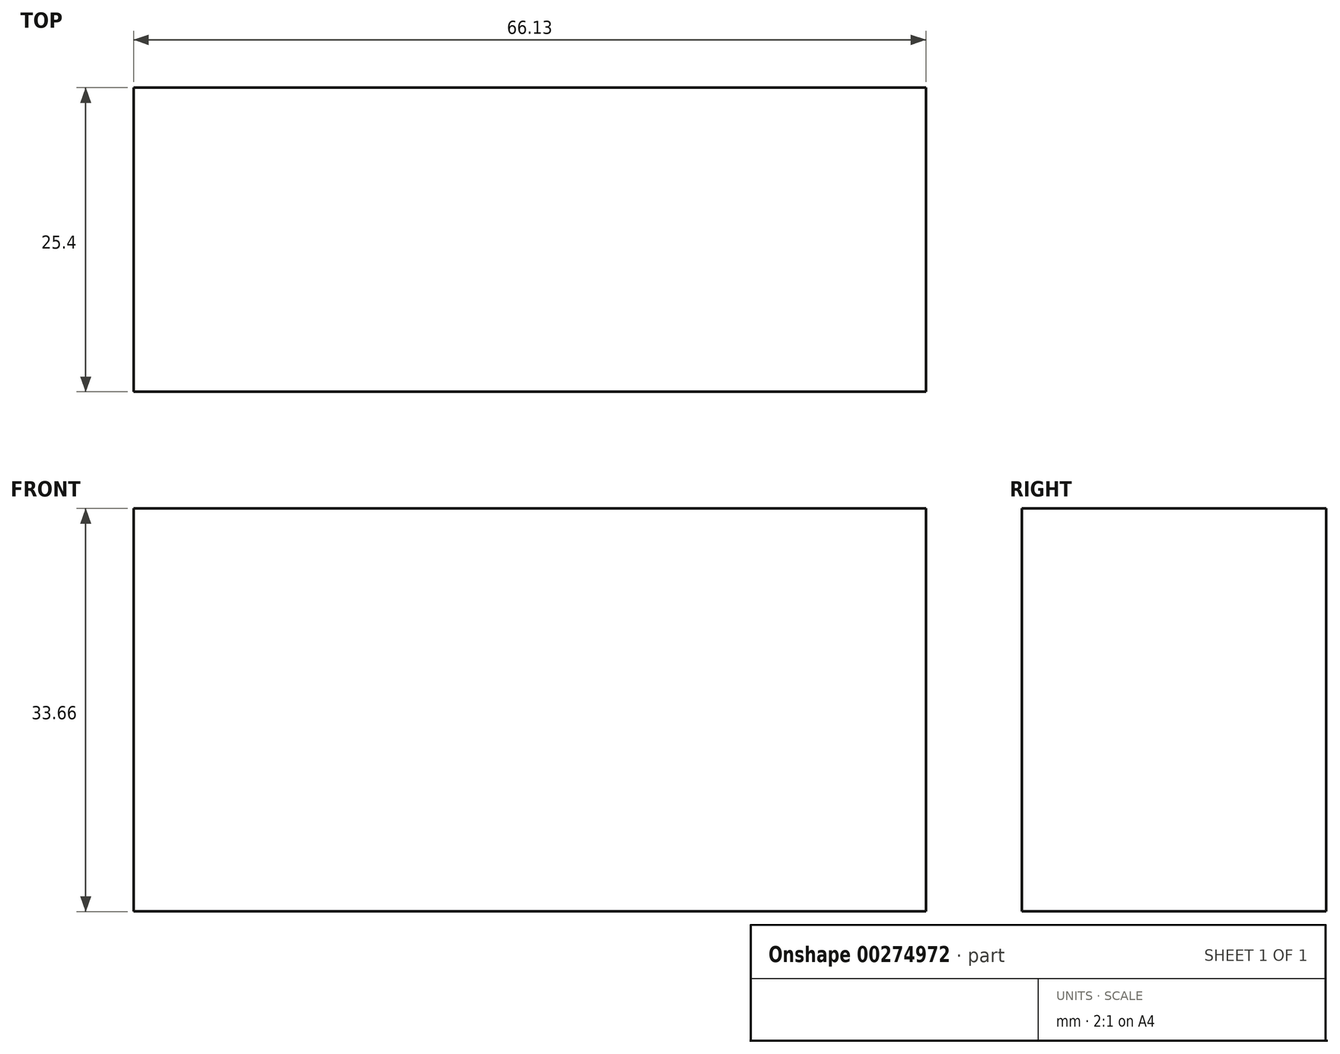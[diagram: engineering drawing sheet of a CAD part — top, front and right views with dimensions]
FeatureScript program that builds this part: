
annotation { "Feature Type Name" : "Feature", "Feature Type Description" : "" }
export const myFeature = defineFeature(function(context is Context, id is Id, definition is map)
    precondition{}
    {
        {
            var Q0;
            Q0=qCreatedBy(makeId("Front.planeOp"),FACE);
            var sketch = newSketch(context, id + "F0", { "sketchPlane" : qUnion([Q0])});
            skLineSegment(sketch, "E0.bottom", {"start": v(-10.04, 17.71) * mm, "end": v(-76.17, 17.71) * mm});
            skLineSegment(sketch, "E0.top", {"start": v(-10.04, 51.37) * mm, "end": v(-76.17, 51.37) * mm});
            skLineSegment(sketch, "E0.left", {"start": v(-10.04, 17.71) * mm, "end": v(-10.04, 51.37) * mm});
            skLineSegment(sketch, "E0.right", {"start": v(-76.17, 17.71) * mm, "end": v(-76.17, 51.37) * mm});
            skPoint(sketch, "E0.middle", {"position": v(-43.1, 34.54) * mm});
            skSolve(sketch);
        }
        {
            var Q0;
            Q0=makeQuery(id+"F0.imprint","IMPRINT",FACE,{"disambiguationData":[TD([[makeQuery(id+"F0.imprint","IMPRINT",EDGE,{"derivedFrom":sQuery(id+"F0.wireOp",EDGE,"E0.bottom")}),-1.0]])]});
            extrude(context, id + "F1", {"entities" : qUnion([Q0]), "oppositeDirection" : true, "depth" : 25.4 * mm});
        }
        {
            var Q0;
            Q0=makeQuery(id+"F1.opExtrude","CAP_FACE",FACE,{"disambiguationData":[OSD([sQuery(id+"F0.wireOp",EDGE,"E0.bottom"),sQuery(id+"F0.wireOp",EDGE,"E0.top"),sQuery(id+"F0.wireOp",EDGE,"E0.left"),sQuery(id+"F0.wireOp",EDGE,"E0.right")])],"isStart":true});
            var sketch = newSketch(context, id + "F2", { "sketchPlane" : qUnion([Q0])});
            skCircle(sketch, "E1", {"center": v(-45.95, 34.4) * mm, "radius": 7.93 * mm});
            skSolve(sketch);
        }
    });
